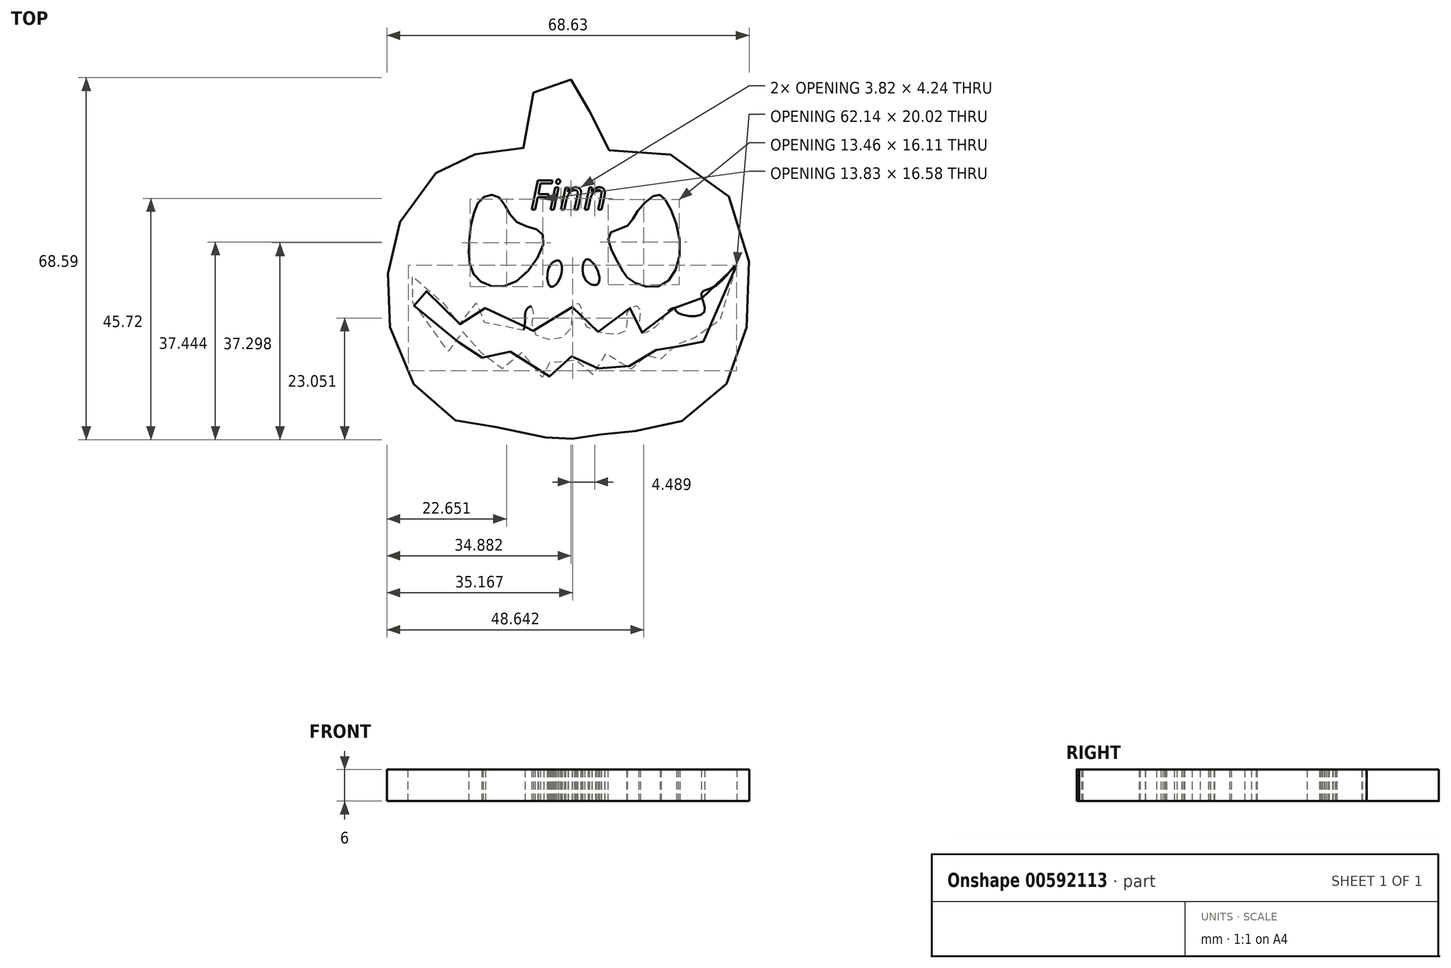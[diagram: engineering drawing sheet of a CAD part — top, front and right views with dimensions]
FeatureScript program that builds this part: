
annotation { "Feature Type Name" : "Feature", "Feature Type Description" : "" }
export const myFeature = defineFeature(function(context is Context, id is Id, definition is map)
    precondition{}
    {
        {
            var Q0;
            Q0=qCreatedBy(makeId("Top.planeOp"),FACE);
            var sketch = newSketch(context, id + "F0", { "sketchPlane" : qUnion([Q0])});
            skFitSpline(sketch, "E0", {"points": [v(-4.96, 47.91) * mm, v(-11.5, 46.78) * mm, v(-13.74, 35.27) * mm, v(-22.45, 33.78) * mm, v(-28.8, 31.72) * mm, v(-37.1, 21.56) * mm, v(-39.68, 11.05) * mm, v(-39.04, 0) * mm, v(-32.4, -12.77) * mm, v(-24.24, -17.49) * mm, v(-17.8, -18.12) * mm, v(-9.06, -19.87) * mm, v(-7.68, -19.38) * mm, v(-3.22, -20.29) * mm, v(0, -19.16) * mm, v(2.17, -19.86) * mm, v(8.37, -18.34) * mm, v(16.95, -16.42) * mm, v(26.2, -6.76) * mm, v(28.7, 7.2) * mm, v(25.87, 24.36) * mm, v(10.38, 34.5) * mm, v(0, 35.54) * mm, v(-1.98, 45.35) * mm, v(-4.96, 47.91) * mm]});
            skFitSpline(sketch, "E1", {"points": [v(-10.3, 18.55) * mm, v(-15.23, 20.9) * mm, v(-18.66, 25.63) * mm, v(-21.87, 25.41) * mm, v(-24.23, 17.9) * mm, v(-22.95, 10.4) * mm, v(-15.66, 9.54) * mm, v(-10.3, 18.55) * mm]});
            skFitSpline(sketch, "E2", {"points": [v(12.87, 25.2) * mm, v(11.15, 26.06) * mm, v(7.5, 22.84) * mm, v(5.36, 20.05) * mm, v(2.14, 18.55) * mm, v(4.07, 12.97) * mm, v(6.22, 9.97) * mm, v(12, 8.9) * mm, v(15.66, 15.76) * mm, v(12.87, 25.2) * mm]});
            skFitSpline(sketch, "E3", {"points": [v(26.38, 12.76) * mm, v(21.87, 0) * mm, v(18.87, -1.6) * mm, v(17.59, 0) * mm, v(15.01, -1.82) * mm, v(15.23, -3.97) * mm, v(12, -5.04) * mm, v(12, -3.54) * mm, v(9.65, -3.97) * mm, v(8.8, -6.76) * mm, v(6.43, -6.97) * mm, v(5.36, -4.83) * mm, v(0, -4.61) * mm, v(0, -7.4) * mm, v(-4.07, -7.83) * mm, v(-4.07, -5.04) * mm, v(-8.15, -4.83) * mm, v(-9, -6.33) * mm, v(-8.36, -7.83) * mm, v(-11.15, -8.26) * mm, v(-13.3, -4.4) * mm, v(-17.37, -4.18) * mm, v(-18.23, -7.18) * mm, v(-21.66, -5.47) * mm, v(-21.87, -1.82) * mm, v(-25.74, 0) * mm, v(-26.6, -3.32) * mm, v(-32.38, 0) * mm, v(-35.81, 11.47) * mm, v(-33.67, 8.9) * mm, v(-28.74, 5.04) * mm, v(-27.88, 2.47) * mm, v(-24.88, 1.82) * mm, v(-23.38, 5.25) * mm, v(-21.23, 5.47) * mm, v(-21.45, 2.04) * mm, v(-14.37, 0) * mm, v(-13.51, 4.18) * mm, v(-12.22, 4.83) * mm, v(-12, 0) * mm, v(-5.36, 0) * mm, v(-4.5, 5.47) * mm, v(-3, 5.04) * mm, v(-2.79, 1.82) * mm, v(5.15, 0) * mm, v(5.58, 2.9) * mm, v(6.43, 4.83) * mm, v(7.93, 4.83) * mm, v(7.93, 2.25) * mm, v(8.36, 0) * mm, v(12, 2.04) * mm, v(13.51, 4.18) * mm, v(14.58, 4.61) * mm, v(15.23, 3.75) * mm, v(20.16, 3.75) * mm, v(19.73, 7.4) * mm, v(22.52, 8.9) * mm, v(26.38, 12.76) * mm]});
            skFitSpline(sketch, "E4", {"points": [v(-7.3, 13.62) * mm, v(-6.86, 10.83) * mm, v(-8.8, 8.69) * mm, v(-9.22, 12.12) * mm, v(-7.3, 13.62) * mm]});
            skFitSpline(sketch, "E5", {"points": [v(-2.14, 13.83) * mm, v(0, 11.9) * mm, v(0, 9.11) * mm, v(-2.36, 10.19) * mm, v(-2.14, 13.83) * mm]});
            skText(sketch, "E6", { "text": "Finn", "fontName": "OpenSans-Italic.ttf"});
            const initialGuessF0  = {"E6": [-0.01276, 0.0233, 1, 0, 0.0056]};
            skSetInitialGuess(sketch, initialGuessF0);
            skSolve(sketch);
        }
        {
            var Q0;
            Q0 = qSketchRegion(id + "F0", true);
            extrude(context, id + "F1", {"entities" : qUnion([Q0]), "depth" : 6 * mm, "offsetDistance" : 25 * mm});
        }
    });
